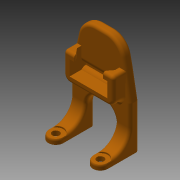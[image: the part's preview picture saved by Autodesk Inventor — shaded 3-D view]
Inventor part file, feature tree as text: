
AUTODESK INVENTOR PART (.ipt)
format: ipt  version: 2014 (Build 180170000, 170)  size: 452,096 bytes
history: native  units: in
note: dims shown in document units (in); Inventor stores cm internally (conversion verified against a paired STEP export)
features: fillet x13, extrude x8, sketch x8, projected_geometry x3
ambient origin geometry x8: Origin, YZ Plane, XZ Plane, XY Plane, X Axis, Y Axis, Z Axis, Center Point
bodies: Solid1 (feature_tree)
feature tree (32):
  extrude  "Extrusion1"  Depth=0.25in
  extrude  "Extrusion2"  Depth=0.15in TaperAngle=0.0deg
  extrude  "Extrusion3"  Depth=0.12in
  fillet  "Fillet1"  Radius=0.1in
  extrude  "Extrusion5"  Depth=0.638in
  extrude  "Extrusion6"  Depth=0.1in
  extrude  "Extrusion7"  Depth=0.081in
  extrude  "Extrusion8"  Depth=0.35in
  fillet  "Fillet19"  Radius=0.45in
  fillet  "Fillet20"  Radius=0.2in
  fillet  "Fillet21"  Radius=0.035in
  fillet  "Fillet22"  Radius=0.05in
  fillet  "Fillet23"  Radius=0.075in
  fillet  "Fillet24"  Radius=0.075in
  fillet  "Fillet25"  Radius=0.075in
  fillet  "Fillet26"  Radius=0.03in
  fillet  "Fillet27"  Radius=0.1in
  fillet  "Fillet28"  Radius=0.1in
  extrude  "Extrusion9"  Depth=0.5in
  fillet  "Fillet30"  Radius=0.65in
  fillet  "Fillet31"  Radius=0.05in
  sketch  "Sketch1"  dims[d4=1.5in d5=0.25in]
  sketch  "Sketch2"  dims[d7=0.25in d9=0.15in d10=0.0in]
  projected_geometry  "Projected Loop1"
  sketch  "Sketch3"  dims[d12=0.1in d13=0.0in d14=0.12in d15=0.1in d16=0.0in]
  projected_geometry  "Projected Loop2"
  sketch  "Sketch5"  dims[d18=0.3in d24=0.638in]
  sketch  "Sketch6"  dims[d25=0.1in d26=0.1in]
  sketch  "Sketch7"  dims[d27=0.1in d28=0.081in]
  projected_geometry  "Projected Loop4"
  sketch  "Sketch8"  dims[d29=0.081in d30=0.35in d31=0.45in d32=0.2in d33=0.0in d34=0.035in d35=0.05in d36=0.075in d37=0.0in d38=0.075in d39=0.075in d40=0.03in d41=0.1in d42=0.0in d43=0.1in d44=0.0in]
  sketch  "Sketch9"  dims[d53=0.5in d54=0.5in d61=0.65in d63=0.05in d64=0.05in d65=0.3in d66=0.05in d67=0.05in d68=0.05in d69=0.05in d70=0.1in d71=0.1in d72=0.05in d73=0.04in d74=0.0in d76=0.1in d77=0.02in d78=0.0in d79=0.005in]
